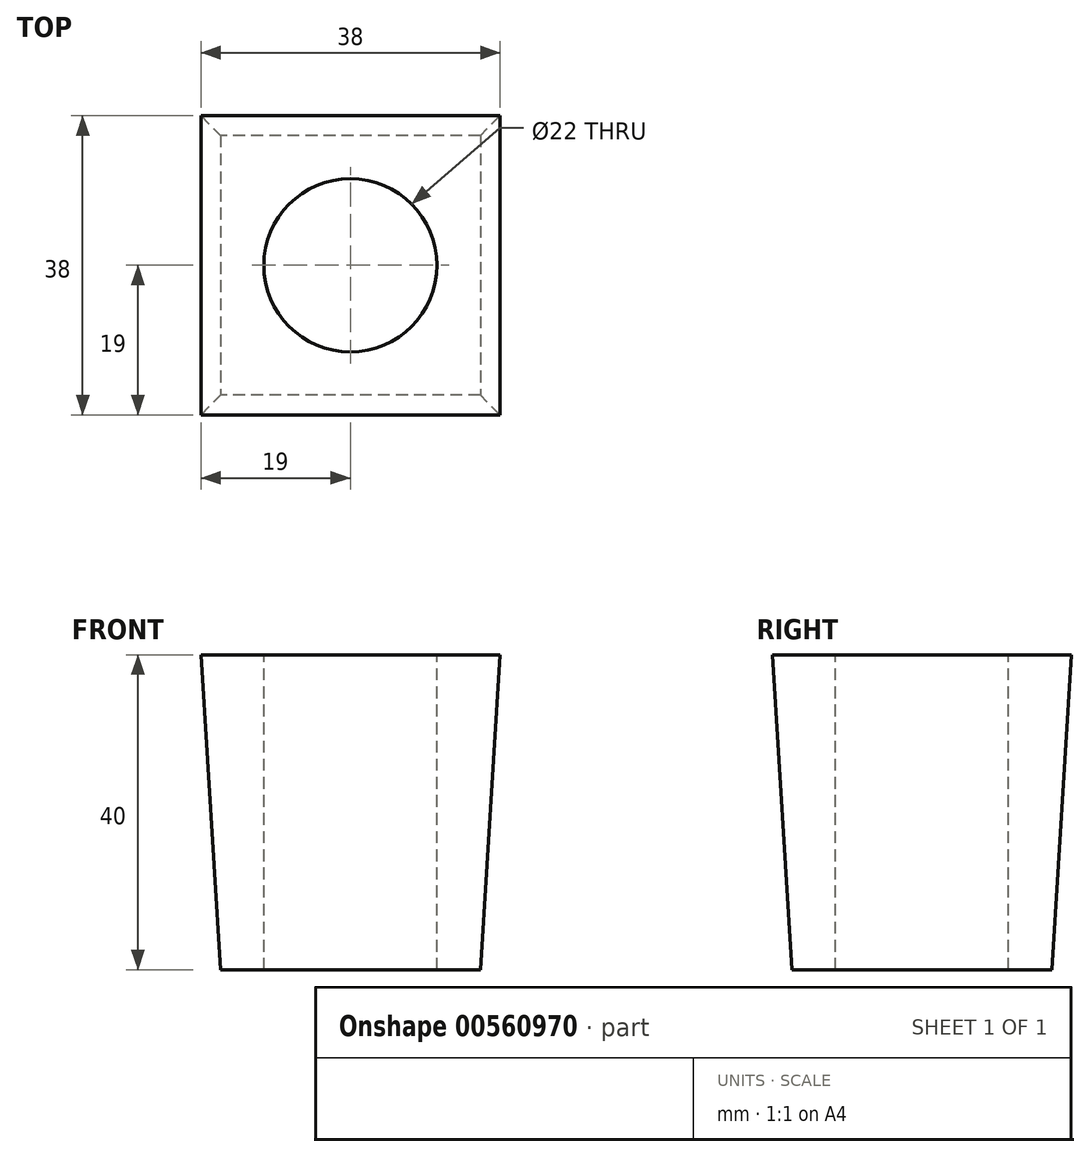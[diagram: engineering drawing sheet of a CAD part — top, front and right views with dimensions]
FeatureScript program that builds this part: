
annotation { "Feature Type Name" : "Feature", "Feature Type Description" : "" }
export const myFeature = defineFeature(function(context is Context, id is Id, definition is map)
    precondition{}
    {
        {
            var Q0;
            Q0=qCreatedBy(makeId("Top.planeOp"),FACE);
            var sketch = newSketch(context, id + "F0", { "sketchPlane" : qUnion([Q0])});
            skLineSegment(sketch, "E0.bottom", {"start": v(16.5, 16.5) * mm, "end": v(-16.5, 16.5) * mm});
            skLineSegment(sketch, "E0.top", {"start": v(16.5, -16.5) * mm, "end": v(-16.5, -16.5) * mm});
            skLineSegment(sketch, "E0.left", {"start": v(16.5, 16.5) * mm, "end": v(16.5, -16.5) * mm});
            skLineSegment(sketch, "E0.right", {"start": v(-16.5, 16.5) * mm, "end": v(-16.5, -16.5) * mm});
            skPoint(sketch, "E0.middle", {"position": v(0, 0) * mm});
            skSolve(sketch);
        }
        {
            var Q0;
            Q0=qCreatedBy(makeId("Top.planeOp"),FACE);
            cPlane(context, id + "F1", {"entities" : qUnion([Q0]), "cplaneType" : CPlaneType.OFFSET, "offset" : 40 * mm, "width" : 150 * mm, "height" : 150 * mm});
        }
        {
            var Q0;
            Q0=qCreatedBy(id+"F1.planeOp",FACE);
            var sketch = newSketch(context, id + "F2", { "sketchPlane" : qUnion([Q0])});
            skLineSegment(sketch, "E1.bottom", {"start": v(19, 19) * mm, "end": v(-19, 19) * mm});
            skLineSegment(sketch, "E1.top", {"start": v(19, -19) * mm, "end": v(-19, -19) * mm});
            skLineSegment(sketch, "E1.left", {"start": v(19, 19) * mm, "end": v(19, -19) * mm});
            skLineSegment(sketch, "E1.right", {"start": v(-19, 19) * mm, "end": v(-19, -19) * mm});
            skPoint(sketch, "E1.middle", {"position": v(0, 0) * mm});
            skSolve(sketch);
        }
        {
            var Q0;
            Q0=makeQuery(id+"F2.imprint","IMPRINT",FACE,{"disambiguationData":[TD([[makeQuery(id+"F2.imprint","IMPRINT",EDGE,{"derivedFrom":sQuery(id+"F2.wireOp",EDGE,"E1.bottom")}),1.0]])]});
            var Q1;
            Q1=makeQuery(id+"F0.imprint","IMPRINT",FACE,{"disambiguationData":[TD([[makeQuery(id+"F0.imprint","IMPRINT",EDGE,{"derivedFrom":sQuery(id+"F0.wireOp",EDGE,"E0.bottom")}),1.0]])]});
            loft(context, id + "F3", {"sheetProfilesArray" : [{ "sheetProfileEntities" : qUnion([Q0]) }, { "sheetProfileEntities" : qUnion([Q1]) }]});
        }
        {
            var Q0;
            Q0=makeQuery(id+"F3.opLoft","CAP_FACE",FACE,{"disambiguationData":[OSD([makeQuery(id+"F2.imprint","IMPRINT",FACE,{"disambiguationData":[TD([[makeQuery(id+"F2.imprint","IMPRINT",EDGE,{"derivedFrom":sQuery(id+"F2.wireOp",EDGE,"E1.bottom")}),1.0]])]})])],"isStart":true});
            var sketch = newSketch(context, id + "F4", { "sketchPlane" : qUnion([Q0])});
            skPoint(sketch, "E2", {"position": v(0, 0) * mm});
            skSolve(sketch);
        }
        {
            var Q0;
            Q0=sQuery(id+"F4.wireOp",VERTEX,"E2");
            var Q1;
            Q1=makeQuery(id+"F3.opLoft","SWEPT_BODY",BODY,{"disambiguationData":[OSD([makeQuery(id+"F0.imprint","IMPRINT",FACE,{"disambiguationData":[TD([[makeQuery(id+"F0.imprint","IMPRINT",EDGE,{"derivedFrom":sQuery(id+"F0.wireOp",EDGE,"E0.bottom")}),1.0]])]}),makeQuery(id+"F2.imprint","IMPRINT",FACE,{"disambiguationData":[TD([[makeQuery(id+"F2.imprint","IMPRINT",EDGE,{"derivedFrom":sQuery(id+"F2.wireOp",EDGE,"E1.bottom")}),1.0]])]})])]});
            hole(context, id + "F5", {"style" : HoleStyle.SIMPLE, "endStyle" : HoleEndStyle.THROUGH, "holeDiameter" : 22 * mm, "majorDiameter" : 5 * mm, "isTappedThrough" : true, "tappedDepth" : 12 * mm, "tapClearance" : 3, "locations" : qUnion([Q0]), "scope" : qUnion([Q1])});
        }
    });
